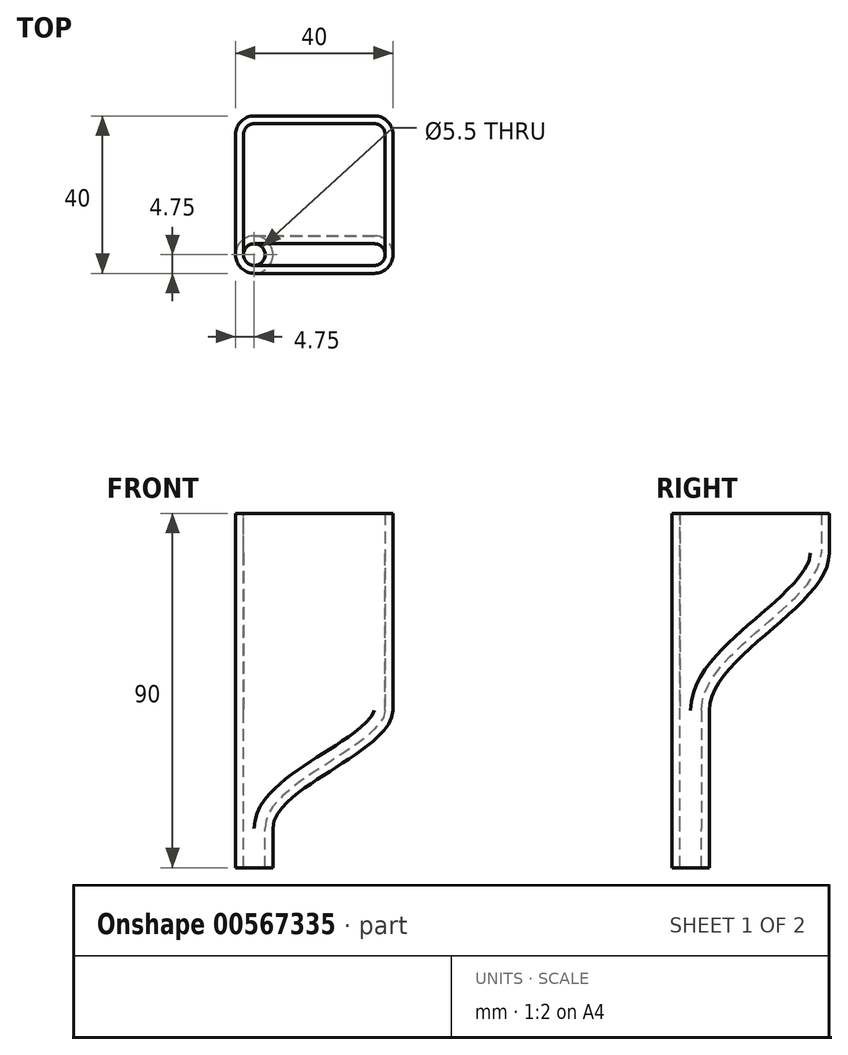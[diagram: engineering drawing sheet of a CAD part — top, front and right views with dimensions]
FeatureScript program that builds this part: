
annotation { "Feature Type Name" : "Feature", "Feature Type Description" : "" }
export const myFeature = defineFeature(function(context is Context, id is Id, definition is map)
    precondition{}
    {
        {
            assignVariable(context, id + "F0", {"name" : "D", "anyValue" : 5});
        }
        {
            assignVariable(context, id + "F1", {"name" : "THICKNESS", "anyValue" : 2});
        }
        {
            assignVariable(context, id + "F2", {"name" : "CLEARANCE", "anyValue" : .5});
        }
        {
            var Q0;
            Q0=qCreatedBy(makeId("Top.planeOp"),FACE);
            cPlane(context, id + "F3", {"entities" : qUnion([Q0]), "cplaneType" : CPlaneType.OFFSET, "offset" : 25 * mm, "width" : 150 * mm, "height" : 150 * mm});
        }
        {
            var Q0;
            Q0=qCreatedBy(id+"F3.planeOp",FACE);
            cPlane(context, id + "F4", {"entities" : qUnion([Q0]), "cplaneType" : CPlaneType.OFFSET, "offset" : 10 * mm, "width" : 150 * mm, "height" : 150 * mm});
        }
        {
            var Q0;
            Q0=qCreatedBy(id+"F4.planeOp",FACE);
            cPlane(context, id + "F5", {"entities" : qUnion([Q0]), "cplaneType" : CPlaneType.OFFSET, "offset" : 30 * mm, "width" : 150 * mm, "height" : 150 * mm});
        }
        {
            var Q0;
            Q0=qCreatedBy(id+"F5.planeOp",FACE);
            cPlane(context, id + "F6", {"entities" : qUnion([Q0]), "cplaneType" : CPlaneType.OFFSET, "offset" : 40 * mm, "width" : 150 * mm, "height" : 150 * mm});
        }
        {
            var Q0;
            Q0=qCreatedBy(id+"F6.planeOp",FACE);
            var sketch = newSketch(context, id + "F7", { "sketchPlane" : qUnion([Q0])});
            skLineSegment(sketch, "E0.bottom", {"start": v(35.25, 35.25) * mm, "end": v(-4.75, 35.25) * mm});
            skLineSegment(sketch, "E0.top", {"start": v(35.25, -4.75) * mm, "end": v(0, -4.75) * mm});
            skLineSegment(sketch, "E0.left", {"start": v(35.25, 35.25) * mm, "end": v(35.25, -4.75) * mm});
            skLineSegment(sketch, "E0.right", {"start": v(-4.75, 35.25) * mm, "end": v(-4.75, 0) * mm});
            skPoint(sketch, "E1.visualSharp", {"position": v(-4.75, -4.75) * mm});
            skArc(sketch, "E1.filletArc", {"start": v(-4.75, 0) * mm, "mid": v(-3.36, -3.36) * mm, "end": v(0, -4.75) * mm});
            skSolve(sketch);
        }
        {
            var Q0;
            Q0=qCreatedBy(id+"F5.planeOp",FACE);
            var sketch = newSketch(context, id + "F8", { "sketchPlane" : qUnion([Q0])});
            skArc(sketch, "E2.0", {"start": v(-4.75, 0) * mm, "mid": v(-3.36, -3.36) * mm, "end": v(0, -4.75) * mm});
            skLineSegment(sketch, "E3.0", {"start": v(35.25, -4.75) * mm, "end": v(0, -4.75) * mm});
            skLineSegment(sketch, "E4.0", {"start": v(-4.75, 4.75) * mm, "end": v(-4.75, 0) * mm});
            skLineSegment(sketch, "E5.0", {"start": v(35.25, 4.75) * mm, "end": v(35.25, -4.75) * mm});
            skLineSegment(sketch, "E6", {"start": v(-4.75, 4.75) * mm, "end": v(35.25, 4.75) * mm});
            skCircle(sketch, "E7", {"center": v(0, 0) * mm, "radius": 4.75 * mm, "construction": true});
            skSolve(sketch);
        }
        {
            var Q0;
            Q0=qCreatedBy(id+"F4.planeOp",FACE);
            var sketch = newSketch(context, id + "F9", { "sketchPlane" : qUnion([Q0])});
            skArc(sketch, "E8.0", {"start": v(-4.75, 0) * mm, "mid": v(-3.36, -3.36) * mm, "end": v(0, -4.75) * mm});
            skLineSegment(sketch, "E9.0", {"start": v(-4.75, 4.75) * mm, "end": v(-4.75, 0) * mm});
            skLineSegment(sketch, "E10.0", {"start": v(-4.75, 4.75) * mm, "end": v(4.75, 4.75) * mm});
            skLineSegment(sketch, "E11.0", {"start": v(4.75, -4.75) * mm, "end": v(0, -4.75) * mm});
            skLineSegment(sketch, "E12", {"start": v(4.75, -4.75) * mm, "end": v(4.75, 4.75) * mm});
            skCircle(sketch, "E13", {"center": v(0, 0) * mm, "radius": 4.75 * mm, "construction": true});
            skSolve(sketch);
        }
        {
            var Q0;
            Q0 = qSketchRegion(id + "F9", true);
            var Q1;
            Q1 = qSketchRegion(id + "F8", true);
            loft(context, id + "F10", {"startCondition" : LoftEndDerivativeType.NORMAL_TO_PROFILE, "startMagnitude" : 1, "endCondition" : LoftEndDerivativeType.NORMAL_TO_PROFILE, "endMagnitude" : 1, "sheetProfilesArray" : [{ "sheetProfileEntities" : qUnion([Q0]) }, { "sheetProfileEntities" : qUnion([Q1]) }]});
        }
        {
            var Q1;
            Q1 = qSketchRegion(id + "F8", true);
            var Q2;
            Q2 = qSketchRegion(id + "F7", true);
            loft(context, id + "F11", {"operationType" : NewBodyOperationType.ADD, "startCondition" : LoftEndDerivativeType.NORMAL_TO_PROFILE, "startMagnitude" : 1, "endCondition" : LoftEndDerivativeType.NORMAL_TO_PROFILE, "endMagnitude" : 1, "sheetProfilesArray" : [{ "sheetProfileEntities" : qUnion([Q1]) }, { "sheetProfileEntities" : qUnion([Q2]) }]});
        }
        {
            var Q0;
            Q0 = qSketchRegion(id + "F9", true);
            var Q1;
            Q1=qCreatedBy(id+"F3.planeOp",FACE);
            extrude(context, id + "F12", {"entities" : qUnion([Q0]), "operationType" : NewBodyOperationType.ADD, "endBound" : BoundingType.UP_TO_SURFACE, "oppositeDirection" : true, "depth" : 25 * mm, "endBoundEntityFace" : qUnion([Q1]), "offsetDistance" : 25 * mm});
        }
        {
            var Q0;
            Q0 = qSketchRegion(id + "F7", true);
            extrude(context, id + "F13", {"entities" : qUnion([Q0]), "operationType" : NewBodyOperationType.ADD, "depth" : 10 * mm, "offsetDistance" : 25 * mm});
        }
        {
            var Q0;
            Q0=makeQuery(id+"F13.opExtrude","SWEPT_EDGE",EDGE,{"disambiguationData":[OSD([sQuery(id+"F7.wireOp",EDGE,"E0.top"),sQuery(id+"F7.wireOp",EDGE,"E0.left")])]});
            var Q1;
            Q1=makeQuery(id+"F13.opExtrude","SWEPT_EDGE",EDGE,{"disambiguationData":[OSD([sQuery(id+"F7.wireOp",EDGE,"E0.bottom"),sQuery(id+"F7.wireOp",EDGE,"E0.left")])]});
            var Q2;
            Q2=makeQuery(id+"F13.opExtrude","SWEPT_EDGE",EDGE,{"disambiguationData":[OSD([sQuery(id+"F7.wireOp",EDGE,"E0.bottom"),sQuery(id+"F7.wireOp",EDGE,"E0.right")])]});
            fillet(context, id + "F14", {"entities" : qUnion([Q0, Q1, Q2]), "radius" : (getVariable(context, 'THICKNESS') + getVariable(context, 'CLEARANCE') / 2 + getVariable(context, 'D') / 2) * mm, "tangentPropagation" : true, "allowEdgeOverflow" : false});
        }
        {
            var Q0;
            Q0=makeQuery(id+"F13.opExtrude","CAP_FACE",FACE,{"disambiguationData":[OSD([sQuery(id+"F7.wireOp",EDGE,"E0.bottom"),sQuery(id+"F7.wireOp",EDGE,"E0.top"),sQuery(id+"F7.wireOp",EDGE,"E0.left"),sQuery(id+"F7.wireOp",EDGE,"E0.right"),sQuery(id+"F7.wireOp",EDGE,"E1.filletArc")])],"isStart":false});
            var Q1;
            Q1=makeQuery(id+"F12.opExtrude","CAP_FACE",FACE,{"disambiguationData":[OSD([sQuery(id+"F9.wireOp",EDGE,"E8.0"),sQuery(id+"F9.wireOp",EDGE,"E9.0"),sQuery(id+"F9.wireOp",EDGE,"E10.0"),sQuery(id+"F9.wireOp",EDGE,"E11.0"),sQuery(id+"F9.wireOp",EDGE,"E12")])],"isStart":false});
            shell(context, id + "F15", {"entities" : qUnion([Q0, Q1]), "thickness" : (getVariable(context, 'THICKNESS')) * mm});
        }
    });
